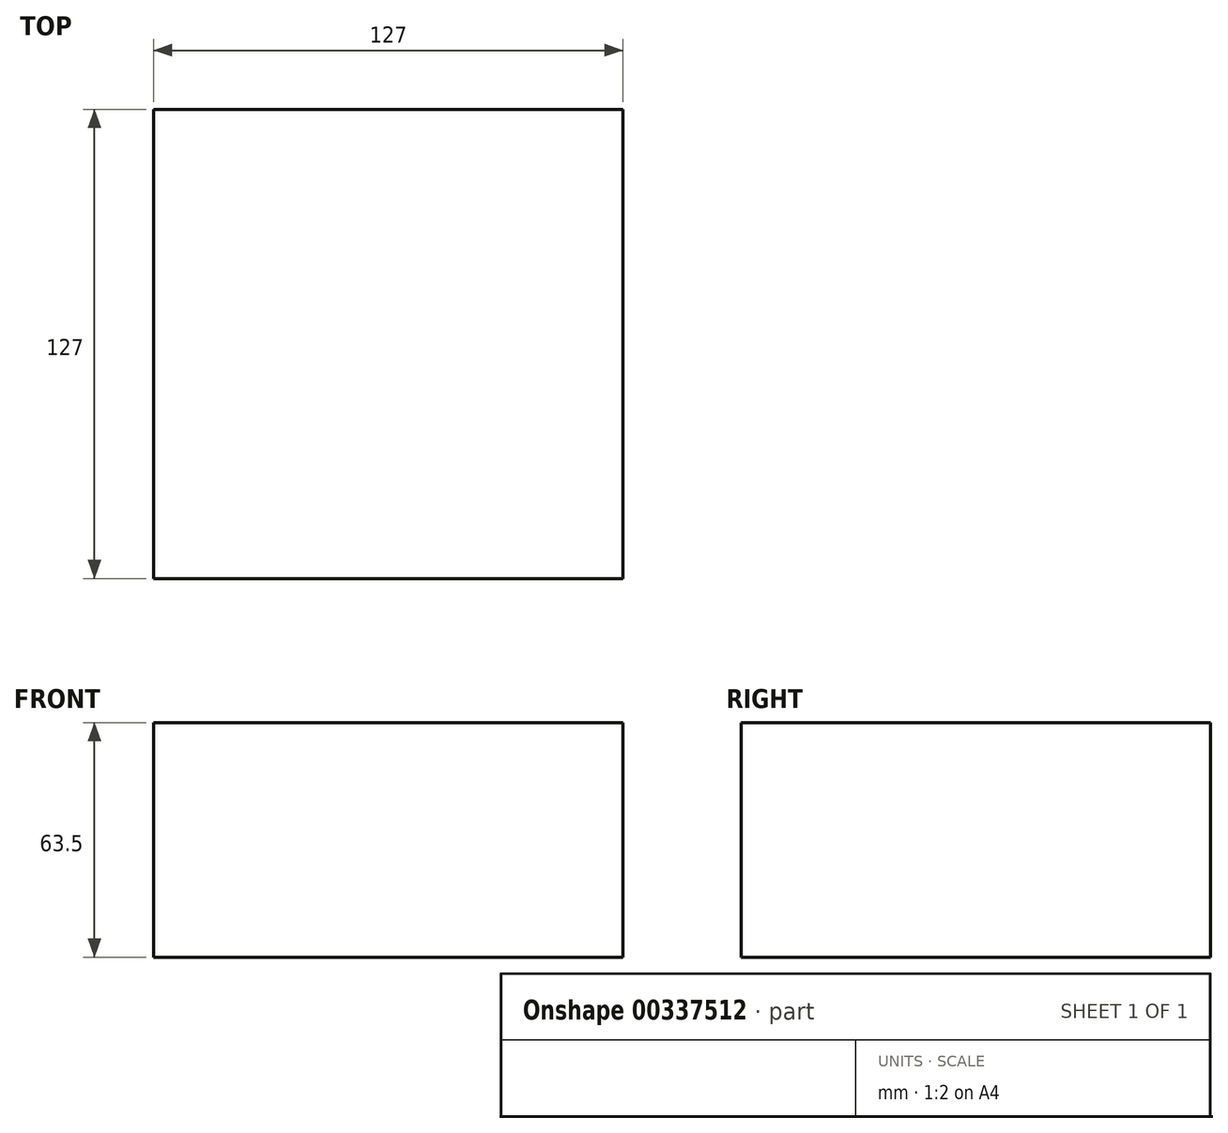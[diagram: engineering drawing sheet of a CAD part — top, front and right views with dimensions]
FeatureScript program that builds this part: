
annotation { "Feature Type Name" : "Feature", "Feature Type Description" : "" }
export const myFeature = defineFeature(function(context is Context, id is Id, definition is map)
    precondition{}
    {
        {
            var Q0;
            Q0=qCreatedBy(makeId("Front.planeOp"),FACE);
            var sketch = newSketch(context, id + "F0", { "sketchPlane" : qUnion([Q0])});
            skLineSegment(sketch, "E0.bottom", {"start": v(63.5, 31.75) * mm, "end": v(-63.5, 31.75) * mm});
            skLineSegment(sketch, "E0.top", {"start": v(63.5, -31.75) * mm, "end": v(-63.5, -31.75) * mm});
            skLineSegment(sketch, "E0.left", {"start": v(63.5, 31.75) * mm, "end": v(63.5, -31.75) * mm});
            skLineSegment(sketch, "E0.right", {"start": v(-63.5, 31.75) * mm, "end": v(-63.5, -31.75) * mm});
            skPoint(sketch, "E0.middle", {"position": v(0, 0) * mm});
            skSolve(sketch);
        }
        {
            var Q0;
            Q0=makeQuery(id+"F0.imprint","IMPRINT",FACE,{"disambiguationData":[TD([[makeQuery(id+"F0.imprint","IMPRINT",EDGE,{"derivedFrom":sQuery(id+"F0.wireOp",EDGE,"E0.bottom")}),1.0]])]});
            extrude(context, id + "F1", {"entities" : qUnion([Q0]), "endBound" : BoundingType.SYMMETRIC, "depth" : 127 * mm});
        }
    });
